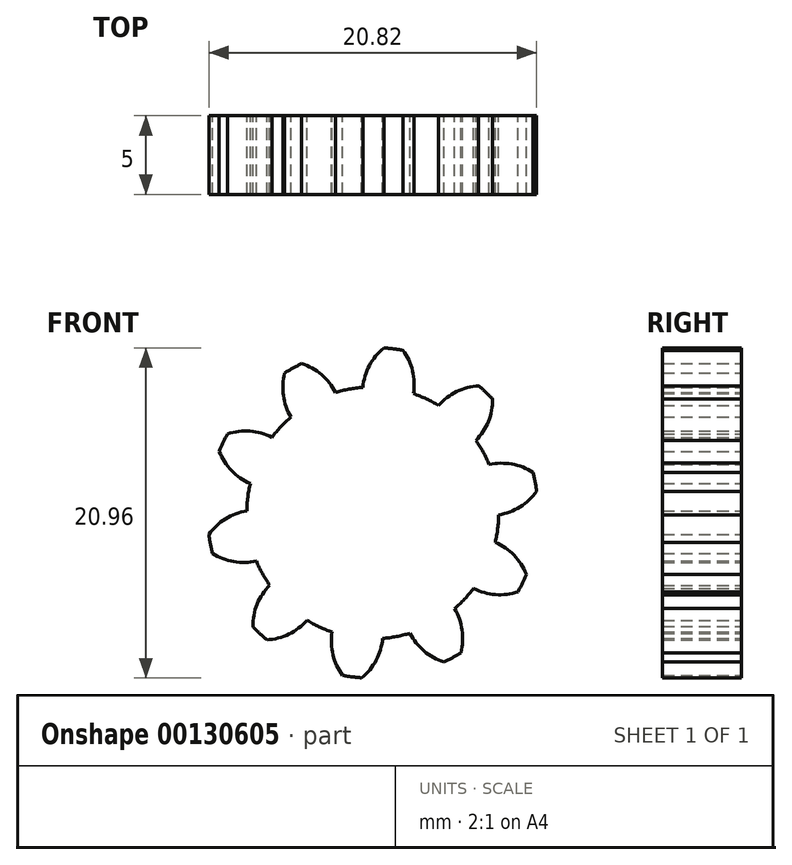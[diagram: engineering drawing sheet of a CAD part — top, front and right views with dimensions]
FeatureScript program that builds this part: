
annotation { "Feature Type Name" : "Feature", "Feature Type Description" : "" }
export const myFeature = defineFeature(function(context is Context, id is Id, definition is map)
    precondition{}
    {
        {
            assignVariable(context, id + "F0", {"name" : "teeth", "anyValue" : 10});
        }
        {
            var Q0;
            Q0=qCreatedBy(makeId("Front.planeOp"),FACE);
            var sketch = newSketch(context, id + "F1", { "sketchPlane" : qUnion([Q0])});
            skCircle(sketch, "E0", {"center": v(0, 0) * mm, "radius": 8.5 * mm, "construction": true});
            skCircle(sketch, "E1", {"center": v(0, 0) * mm, "radius": 10.5 * mm, "construction": true});
            skCircle(sketch, "E2", {"center": v(0, 0) * mm, "radius": 8 * mm});
            skCircle(sketch, "E3", {"center": v(17.03, 0) * mm, "radius": 8 * mm, "construction": true});
            skLineSegment(sketch, "E4", {"start": v(7.52, 2.74) * mm, "end": v(8.51, 0) * mm, "construction": true});
            skLineSegment(sketch, "E5", {"start": v(0, 0) * mm, "end": v(8.51, 0) * mm, "construction": true});
            skLineSegment(sketch, "E6", {"start": v(8.51, 0) * mm, "end": v(8.51, 28.46) * mm, "construction": true});
            skLineSegment(sketch, "E7", {"start": v(8.51, 0) * mm, "end": v(9.5, -2.74) * mm, "construction": true});
            skLineSegment(sketch, "E8", {"start": v(8.51, 0) * mm, "end": v(17.03, 0) * mm, "construction": true});
            skLineSegment(sketch, "E9", {"start": v(7.52, 2.74) * mm, "end": v(0, 0) * mm, "construction": true});
            skArc(sketch, "E10", {"start": v(7.52, 2.74) * mm, "mid": v(7.89, 1.33) * mm, "end": v(8, -0.12) * mm, "construction": true});
            skArc(sketch, "E11", {"start": v(8, -0.12) * mm, "mid": v(7.34, 3.19) * mm, "end": v(5.37, 5.93) * mm, "construction": true});
            skLineSegment(sketch, "E12", {"start": v(5.37, 5.93) * mm, "end": v(0, 0) * mm, "construction": true});
            skLineSegment(sketch, "E13", {"start": v(5.37, 5.93) * mm, "end": v(10.41, 1.37) * mm, "construction": true});
            skLineSegment(sketch, "E14", {"start": v(8, -0.12) * mm, "end": v(0, 0) * mm, "construction": true});
            skArc(sketch, "E15", {"start": v(8, -0.12) * mm, "mid": v(9.35, 0.38) * mm, "end": v(10.41, 1.37) * mm});
            skLineSegment(sketch, "E16", {"start": v(0, 0) * mm, "end": v(10.31, 1.97) * mm, "construction": true});
            skArc(sketch, "E17.MirrorCS", {"start": v(7.4, 3.06) * mm, "mid": v(8.83, 3.1) * mm, "end": v(10.18, 2.57) * mm});
            skPoint(sketch, "E18", {"position": v(7.9, 3.14) * mm});
            skArc(sketch, "E19", {"start": v(10.41, 1.37) * mm, "mid": v(10.31, 1.97) * mm, "end": v(10.18, 2.57) * mm});
            skPoint(sketch, "E20", {"position": v(7.86, 1.5) * mm});
            skArc(sketch, "E21", {"start": v(8, -0.12) * mm, "mid": v(7.86, 1.5) * mm, "end": v(7.4, 3.06) * mm});
            skLineSegment(sketch, "E22", {"start": v(0, 0) * mm, "end": v(7.4, 3.06) * mm, "construction": true});
            skSolve(sketch);
        }
        {
            var Q0;
            {var subQ0=sQuery(id+"F1.wireOp",EDGE,"E2");var subQ1=makeQuery(id+"F1.imprint","INTERSECT",VERTEX,{"derivedFrom":[subQ0,sQuery(id+"F1.wireOp",EDGE,"E15")]});Q0=makeQuery(id+"F1.imprint","IMPRINT",FACE,{"disambiguationData":[TD([[makeQuery(id+"F1.imprint","IMPRINT",EDGE,{"disambiguationData":[TD([[subQ1,1.0]])],"derivedFrom":subQ0}),1.0]])]});}
            extrude(context, id + "F2", {"entities" : qUnion([Q0]), "depth" : 5 * mm});
        }
        {
            var Q0;
            {var subQ0=sQuery(id+"F1.wireOp",EDGE,"E15");Q0=makeQuery(id+"F1.imprint","IMPRINT",FACE,{"disambiguationData":[TD([[makeQuery(id+"F1.imprint","IMPRINT",EDGE,{"derivedFrom":subQ0}),1.0]])]});}
            extrude(context, id + "F3", {"entities" : qUnion([Q0]), "depth" : 5 * mm});
        }
        {
            var Q0;
            Q0=qCreatedBy(makeId("Right.planeOp"),FACE);
            var sketch = newSketch(context, id + "F4", { "sketchPlane" : qUnion([Q0])});
            skLineSegment(sketch, "E23", {"start": v(0, 0) * mm, "end": v(12.3, 0) * mm});
            skSolve(sketch);
        }
        {
            var Q0;
            Q0=makeQuery(id+"F3.opExtrude","SWEPT_BODY",BODY,{"disambiguationData":[OSD([sQuery(id+"F1.wireOp",EDGE,"E2"),sQuery(id+"F1.wireOp",EDGE,"E15"),sQuery(id+"F1.wireOp",EDGE,"E17.MirrorCS"),sQuery(id+"F1.wireOp",EDGE,"E19")])]});
            var Q1;
            Q1=sQuery(id+"F4.wireOp",EDGE,"E23");
            circularPattern(context, id + "F5", {"operationType" : NewBodyOperationType.ADD, "entities" : qUnion([Q0]), "axis" : qUnion([Q1]), "angle" : (360 / getVariable(context, 'teeth')) * degree, "instanceCount" : getVariable(context, 'teeth')});
        }
    });
